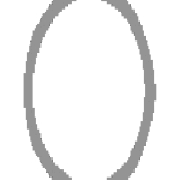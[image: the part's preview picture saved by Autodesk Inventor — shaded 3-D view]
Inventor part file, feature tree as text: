
AUTODESK INVENTOR PART (.ipt)
format: ipt  version: 2021 (Build 250183000, 183)  size: 112,640 bytes
history: native  units: in
note: dims shown in document units (in); Inventor stores cm internally (conversion verified against a paired STEP export)
features: other x4, sketch x3, plane x1
ambient origin geometry x8: Origin, YZ Plane, XZ Plane, XY Plane, X Axis, Y Axis, Z Axis, Center Point
bodies: Solid1 (feature_tree), Body (feature_tree)
feature tree (8):
  other  "Driven Length"
  other  "Frame Generator"
  other  "Start Plane"
  other  "End Plane"
  sketch  "Sketch"  dims[d2=9.0139in d4=-0.0in d5=9.0139in d6=0.12in d7=0.0in d8=90.0deg d9=9.0139in]
  sketch  "Sketch2"  dims[d0=1.0in]
  plane  "Work Plane3"
  sketch  "Sketch3"  dims[d1=0.065in]
